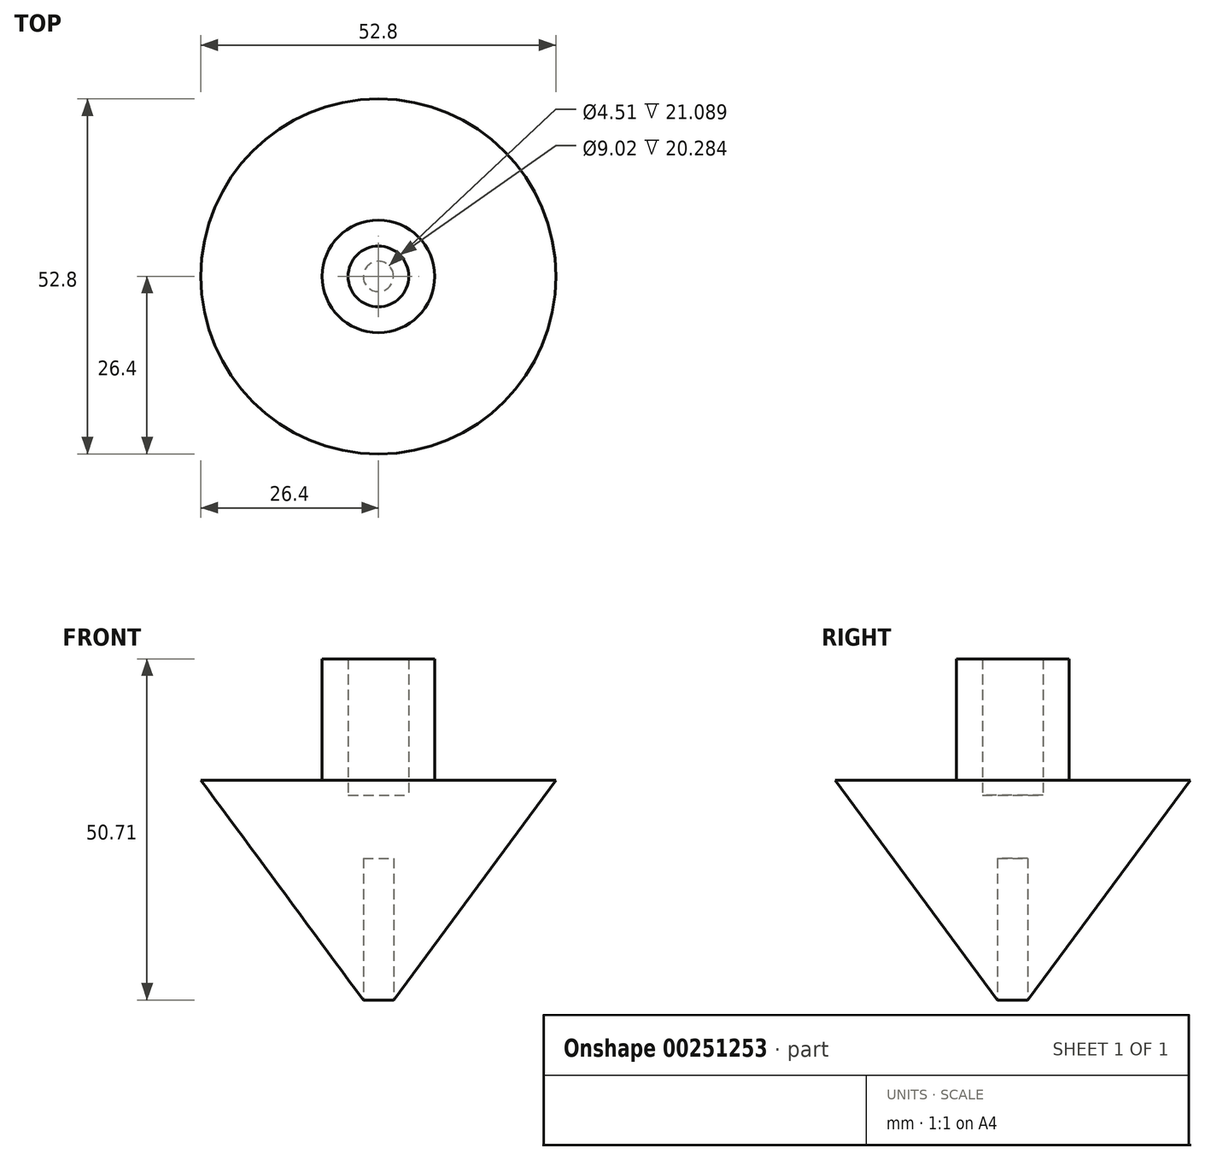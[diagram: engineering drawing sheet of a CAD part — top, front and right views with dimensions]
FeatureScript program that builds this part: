
annotation { "Feature Type Name" : "Feature", "Feature Type Description" : "" }
export const myFeature = defineFeature(function(context is Context, id is Id, definition is map)
    precondition{}
    {
        {
            var Q0;
            Q0=qCreatedBy(makeId("Front.planeOp"),FACE);
            var sketch = newSketch(context, id + "F0", { "sketchPlane" : qUnion([Q0])});
            skLineSegment(sketch, "E0", {"start": v(0, 0) * mm, "end": v(2.25, 0) * mm});
            skLineSegment(sketch, "E1", {"start": v(2.25, 0) * mm, "end": v(2.25, 21.09) * mm});
            skLineSegment(sketch, "E2", {"start": v(2.25, 21.09) * mm, "end": v(0, 21.09) * mm});
            skLineSegment(sketch, "E3", {"start": v(0, 21.09) * mm, "end": v(0, 30.43) * mm});
            skLineSegment(sketch, "E4", {"start": v(0, 30.43) * mm, "end": v(4.5, 30.43) * mm});
            skLineSegment(sketch, "E5", {"start": v(4.5, 30.43) * mm, "end": v(4.5, 50.71) * mm});
            skLineSegment(sketch, "E6", {"start": v(4.5, 50.71) * mm, "end": v(8.37, 50.71) * mm});
            skLineSegment(sketch, "E7", {"start": v(8.37, 50.71) * mm, "end": v(8.37, 32.68) * mm});
            skLineSegment(sketch, "E8", {"start": v(8.37, 32.68) * mm, "end": v(26.4, 32.68) * mm});
            skLineSegment(sketch, "E9", {"start": v(26.4, 32.68) * mm, "end": v(2.25, 0) * mm});
            skSolve(sketch);
        }
        {
            var Q0;
            Q0=makeQuery(id+"F0.imprint","IMPRINT",FACE,{"disambiguationData":[TD([[makeQuery(id+"F0.imprint","IMPRINT",EDGE,{"derivedFrom":sQuery(id+"F0.wireOp",EDGE,"E1")}),-1.0]])]});
            var Q1;
            Q1=sQuery(id+"F0.wireOp",EDGE,"E3");
            revolve(context, id + "F1", {"entities" : qUnion([Q0]), "axis" : qUnion([Q1]), "revolveType" : RevolveType.FULL});
        }
    });
